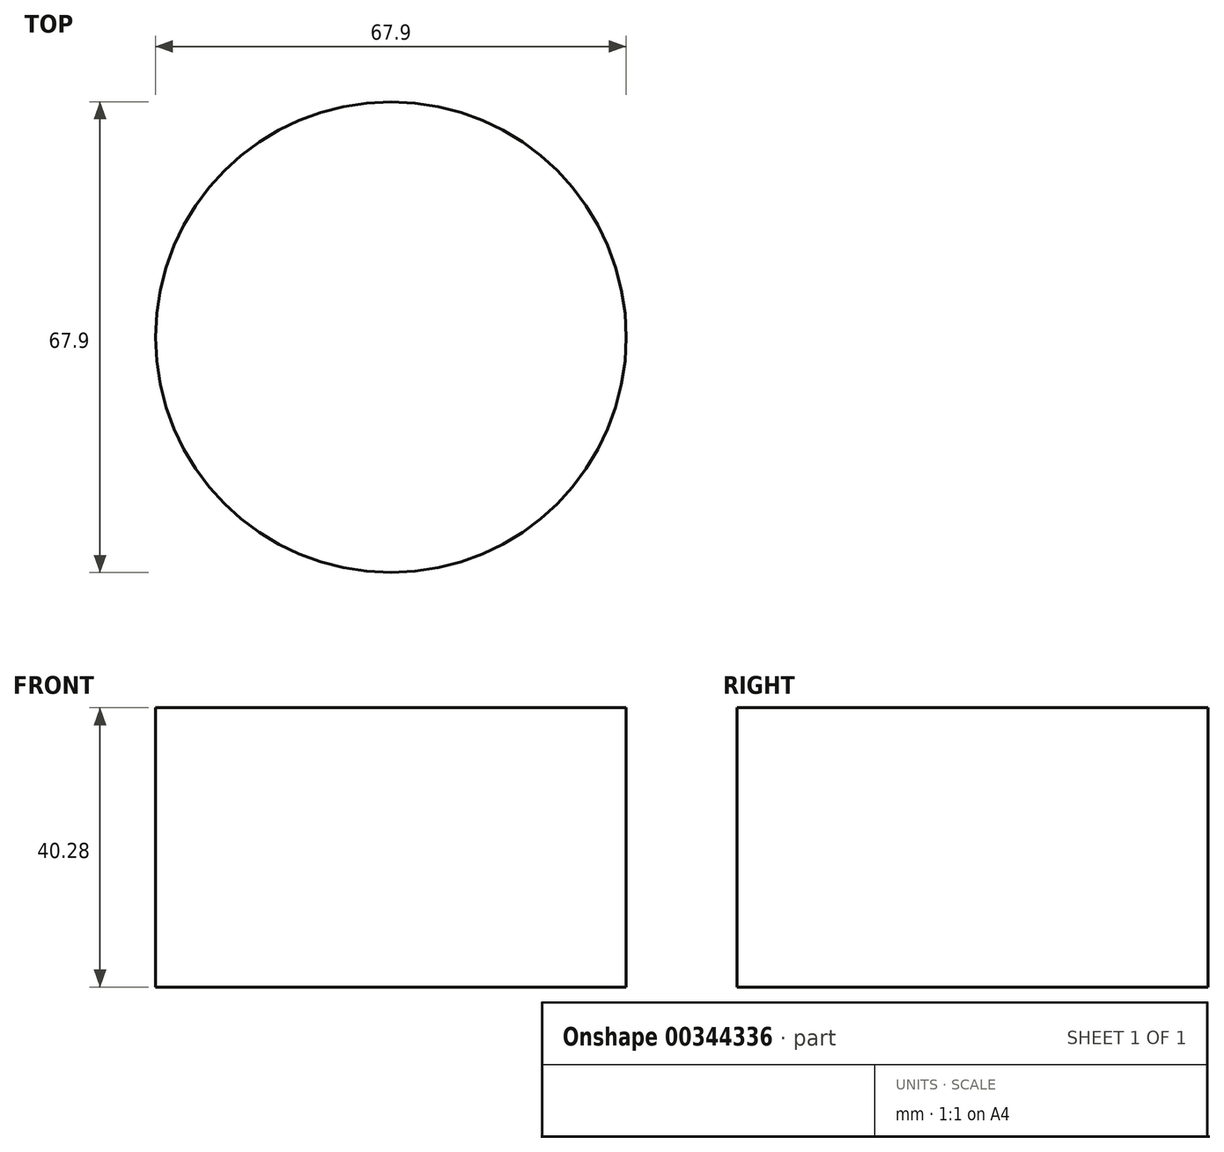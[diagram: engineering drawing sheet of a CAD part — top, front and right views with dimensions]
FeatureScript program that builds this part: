
annotation { "Feature Type Name" : "Feature", "Feature Type Description" : "" }
export const myFeature = defineFeature(function(context is Context, id is Id, definition is map)
    precondition{}
    {
        {
            var Q0;
            Q0=qCreatedBy(makeId("Top.planeOp"),FACE);
            var sketch = newSketch(context, id + "F0", { "sketchPlane" : qUnion([Q0])});
            skCircle(sketch, "E0", {"center": v(0, 0) * mm, "radius": 33.95 * mm});
            skSolve(sketch);
        }
        {
            var Q0;
            Q0=makeQuery(id+"F0.imprint","IMPRINT",FACE,{"disambiguationData":[TD([[makeQuery(id+"F0.imprint","IMPRINT",EDGE,{"derivedFrom":sQuery(id+"F0.wireOp",EDGE,"E0")}),1.0]])]});
            extrude(context, id + "F1", {"entities" : qUnion([Q0]), "oppositeDirection" : true, "depth" : 40.28 * mm});
        }
    });
